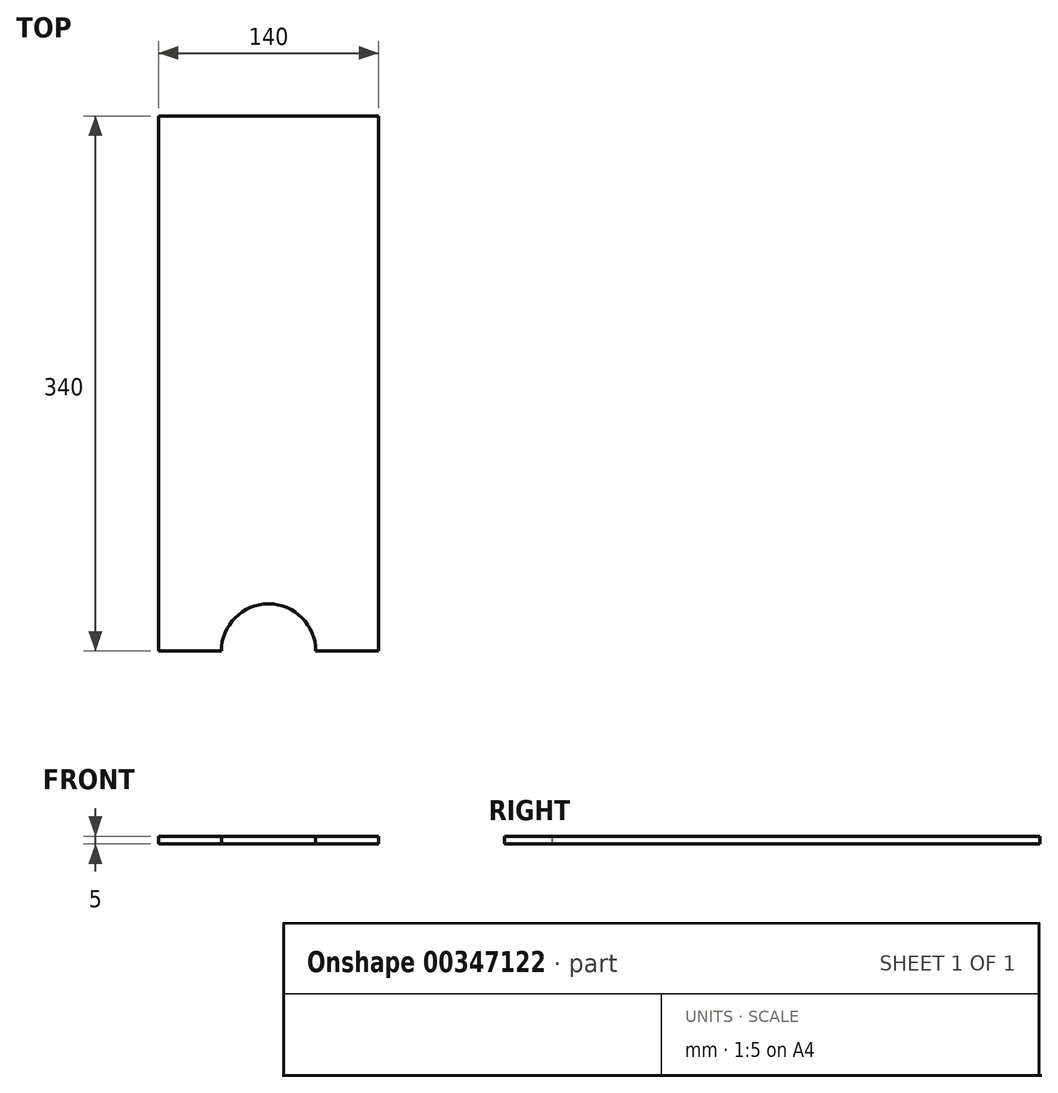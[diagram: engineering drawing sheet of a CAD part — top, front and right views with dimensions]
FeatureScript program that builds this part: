
annotation { "Feature Type Name" : "Feature", "Feature Type Description" : "" }
export const myFeature = defineFeature(function(context is Context, id is Id, definition is map)
    precondition{}
    {
        {
            var Q0;
            Q0=qCreatedBy(makeId("Top.planeOp"),FACE);
            var sketch = newSketch(context, id + "F0", { "sketchPlane" : qUnion([Q0])});
            skLineSegment(sketch, "E0.bottom", {"start": v(-70, 170) * mm, "end": v(70, 170) * mm});
            skLineSegment(sketch, "E0.left", {"start": v(-70, 170) * mm, "end": v(-70, -170) * mm});
            skLineSegment(sketch, "E0.right", {"start": v(70, 170) * mm, "end": v(70, -170) * mm});
            skPoint(sketch, "E0.middle", {"position": v(0, 0) * mm});
            skArc(sketch, "E1", {"start": v(30, -170) * mm, "mid": v(0, -140) * mm, "end": v(-30, -170) * mm});
            skLineSegment(sketch, "E2", {"start": v(-70, -170) * mm, "end": v(-30, -170) * mm});
            skLineSegment(sketch, "E3", {"start": v(70, -170) * mm, "end": v(30, -170) * mm});
            skSolve(sketch);
        }
        {
            var Q0;
            Q0=qSketchRegion(id+"F0",true);
            extrude(context, id + "F1", {"entities" : qUnion([Q0]), "depth" : 5 * mm});
        }
    });
